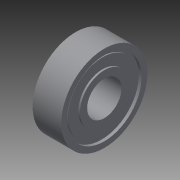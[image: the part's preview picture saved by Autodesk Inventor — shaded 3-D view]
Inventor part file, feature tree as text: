
AUTODESK INVENTOR PART (.ipt)
format: ipt  version: 2015 (Build 190159000, 159)  size: 129,536 bytes
history: native  units: mm
features: sketch x2, revolve x1, extrude x1
ambient origin geometry x8: Origin, YZ Plane, XZ Plane, XY Plane, X Axis, Y Axis, Z Axis, Center Point
bodies: Solid1 (feature_tree)
feature tree (4):
  revolve  "Revolution1"  [1 undecoded]
  extrude  "Extrusion1"  Depth=0.2mm
  sketch  "Sketch1"  dims[d2=4.25mm d3=0.3mm]
  sketch  "Sketch2"  dims[d4=1.8mm d5=0.2mm d6=1.0mm d8=2.5mm d9=7.5mm d10=90.0deg d11=6.0mm d12=5.0mm d13=0.0mm]
note: 1 required parameter value undecoded (feature->parameter linkage not recoverable at this tier; creation-order binding heuristic only, values carry confidence <= 0.55)
